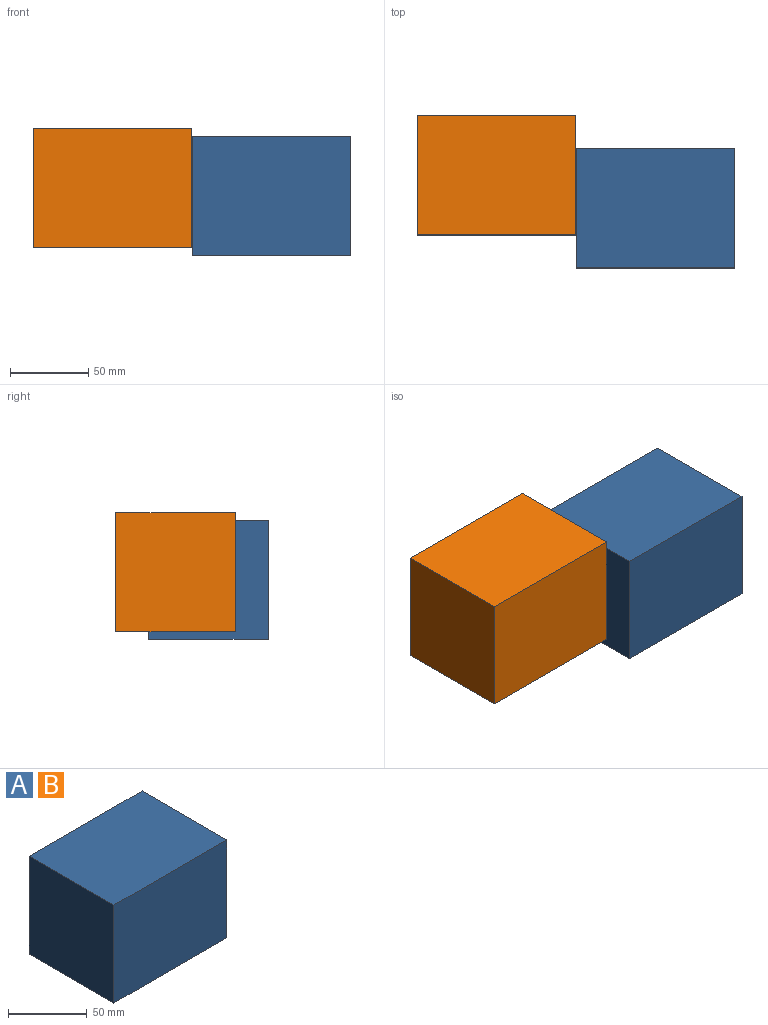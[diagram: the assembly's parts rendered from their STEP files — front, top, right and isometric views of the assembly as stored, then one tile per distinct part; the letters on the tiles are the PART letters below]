
ASSEMBLY  parts=2 mates=1
PART A: 6 faces, bbox 101.6x76.2x76.2 mm
  f0: plane 101.6x76.2mm, normal (0,-1,0), area 7741.9mm2, adj f1,f3,f4,f5
  f1: plane 76.2x76.2mm, normal (1,0,0), area 5806.4mm2, adj f0,f2,f4,f5
  f2: plane 101.6x76.2mm, normal (0,1,0), area 7741.9mm2, adj f1,f3,f4,f5
  f3: plane 76.2x76.2mm, normal (-1,0,0), area 5806.4mm2, adj f0,f2,f4,f5
  f4: plane 101.6x76.2mm, normal (0,0,1), area 7741.9mm2, adj f0,f1,f2,f3
  f5: plane 101.6x76.2mm, normal (0,0,-1), area 7741.9mm2, adj f0,f1,f2,f3
PART B: same geometry as A
PLACE A t=(-47.07,12.13,9.67)mm
PLACE B t=(-148.67,33.24,14.4)mm
MATE planar B.f1 <-> A.f3  axis (1,0,0) through (-97.87,33.24,52.5)mm
